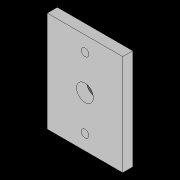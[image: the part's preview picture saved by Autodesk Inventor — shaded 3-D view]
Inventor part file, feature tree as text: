
AUTODESK INVENTOR PART (.ipt)
format: ipt  version: 2021 (Build 250183000, 183)  size: 84,992 bytes
history: native  units: mm
features: reference x7, other x5, plane x1, extrude x1, sketch x1
ambient origin geometry x8: Origin, YZ Plane, XZ Plane, XY Plane, X Axis, Y Axis, Z Axis, Center Point
bodies: Solid1 (feature_tree)
feature tree (15):
  plane  "Work Plane1"
  extrude  "Extrusion1"  [1 undecoded]
  sketch  "Sketch1"  dims[d0=20.0mm d1=0.0mm]
  reference  "Reference1"
  reference  "Reference3"
  reference  "Reference4"
  reference  "Reference5"
  reference  "Reference6"
  reference  "Reference7"
  reference  "Reference8"
  other  "Subensamble_mesa.iam"
  other  "193992 DSNU-32-60-PPS-A---(60PPSA---00--0-------0):2"
  other  "193992 DSNU-32-60-PPS---(A----0-ZR):1"
  other  "Soporte Superior Tubos:1"
  other  "Eje roscado base soporte tubo:1"
note: 1 required parameter value undecoded (feature->parameter linkage not recoverable at this tier; creation-order binding heuristic only, values carry confidence <= 0.55)
